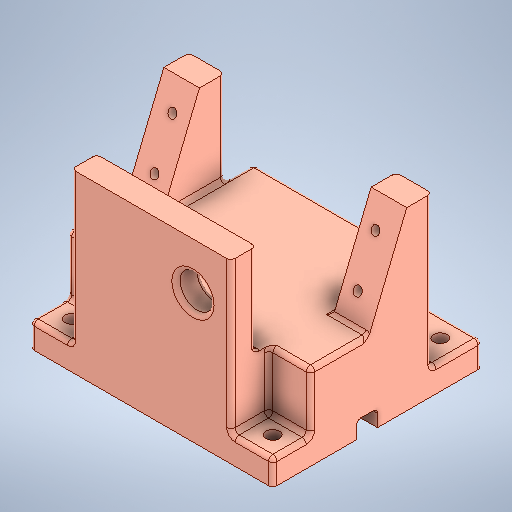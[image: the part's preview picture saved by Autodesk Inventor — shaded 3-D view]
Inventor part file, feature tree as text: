
AUTODESK INVENTOR PART (.ipt)
format: ipt  version: 2025.3 (Build 293356000, 356)  size: 519,168 bytes
history: native  units: in
note: dims shown in document units (in); Inventor stores cm internally (conversion verified against a paired STEP export)
features: sketch x13, extrude x10, fillet x3, plane x2, hole x1
ambient origin geometry x8: Origin, YZ Plane, XZ Plane, XY Plane, X Axis, Y Axis, Z Axis, Center Point
bodies: Solid1 (feature_tree)
feature tree (29):
  extrude  "Extrusion1"  Depth=1.7717in
  extrude  "Extrusion2"  Depth=0.4094in
  extrude  "Extrusion3"  Depth=0.3937in
  extrude  "Extrusion4"  Depth=1.6142in
  extrude  "Extrusion5"  TaperAngle=0.0deg  [1 undecoded]
  extrude  "Extrusion6"  Depth=0.2362in
  plane  "Work Plane1"
  extrude  "Extrusion7"  Depth=0.8661in
  plane  "Work Plane2"
  extrude  "Extrusion8"  Depth=0.4409in
  hole  "Hole1"  [1 undecoded]
  fillet  "Fillet1"  Radius=1.9685in
  extrude  "Extrusion10"  TaperAngle=0.0deg  [1 undecoded]
  sketch  "Sketch10"  dims[d28=0.0in d29=0.126in d30=2.2835in d31=1.9685in]
  extrude  "Extrusion11"  Depth=0.126in
  fillet  "Fillet3"  Radius=2.2835in
  fillet  "Fillet4"  Radius=1.9685in
  sketch  "Sketch1"  dims[d0=2.2835in d1=1.7717in]
  sketch  "Sketch2"  dims[d2=0.8031in d3=0.4094in]
  sketch  "Sketch3"  dims[d7=0.3543in d8=1.6142in]
  sketch  "Sketch4"  dims[d9=0.2756in d10=0.0in d11=0.0in]
  sketch  "Sketch5"  dims[d12=0.2362in d13=0.2362in]
  sketch  "Sketch6"  dims[d14=0.8661in d15=0.0in d16=0.3189in]
  sketch  "Sketch7"  dims[d17=0.357in d18=0.4409in]
  sketch  "Sketch8"  dims[d19=0.0in d20=0.0in d23=0.2362in d24=0.0in d25=1.9685in]
  sketch  "Sketch9"  dims[d26=0.0in d27=0.0in]
  sketch  "Sketch Rectangular Pattern2"  dims[d4=1.6535in d5=0.0in d6=0.3937in]
  sketch  "Sketch12"  dims[d32=0.1969in]
  sketch  "Sketch13"  dims[d33=0.1969in d42=0.0in d43=0.0in d44=-0.1673in d45=0.8661in d46=0.5906in d47=0.3346in d48=0.0in d49=-0.1673in d50=0.2362in d51=0.8661in d52=0.5906in d53=0.3346in d54=0.0in d55=1.9094in d56=0.1772in d57=0.4094in d58=1.0079in d59=0.0787in d60=0.2362in d61=0.1575in d62=0.0787in d63=90.0deg d64=0.315in d65=0.8108in d66=0.0394in d67=1.8898in d68=0.4843in d69=0.6811in d70=0.5433in d71=1.5748in d72=0.7874in d74=1.8898in d75=0.7874in d77=1.5748in d85=0.3937in d86=0.0in d89=0.1969in d90=0.1575in d91=0.7874in d92=0.0in d93=1.4673in d94=0.0in d95=0.0394in d96=0.0394in]
note: 3 required parameter values undecoded (feature->parameter linkage not recoverable at this tier; creation-order binding heuristic only, values carry confidence <= 0.55)
